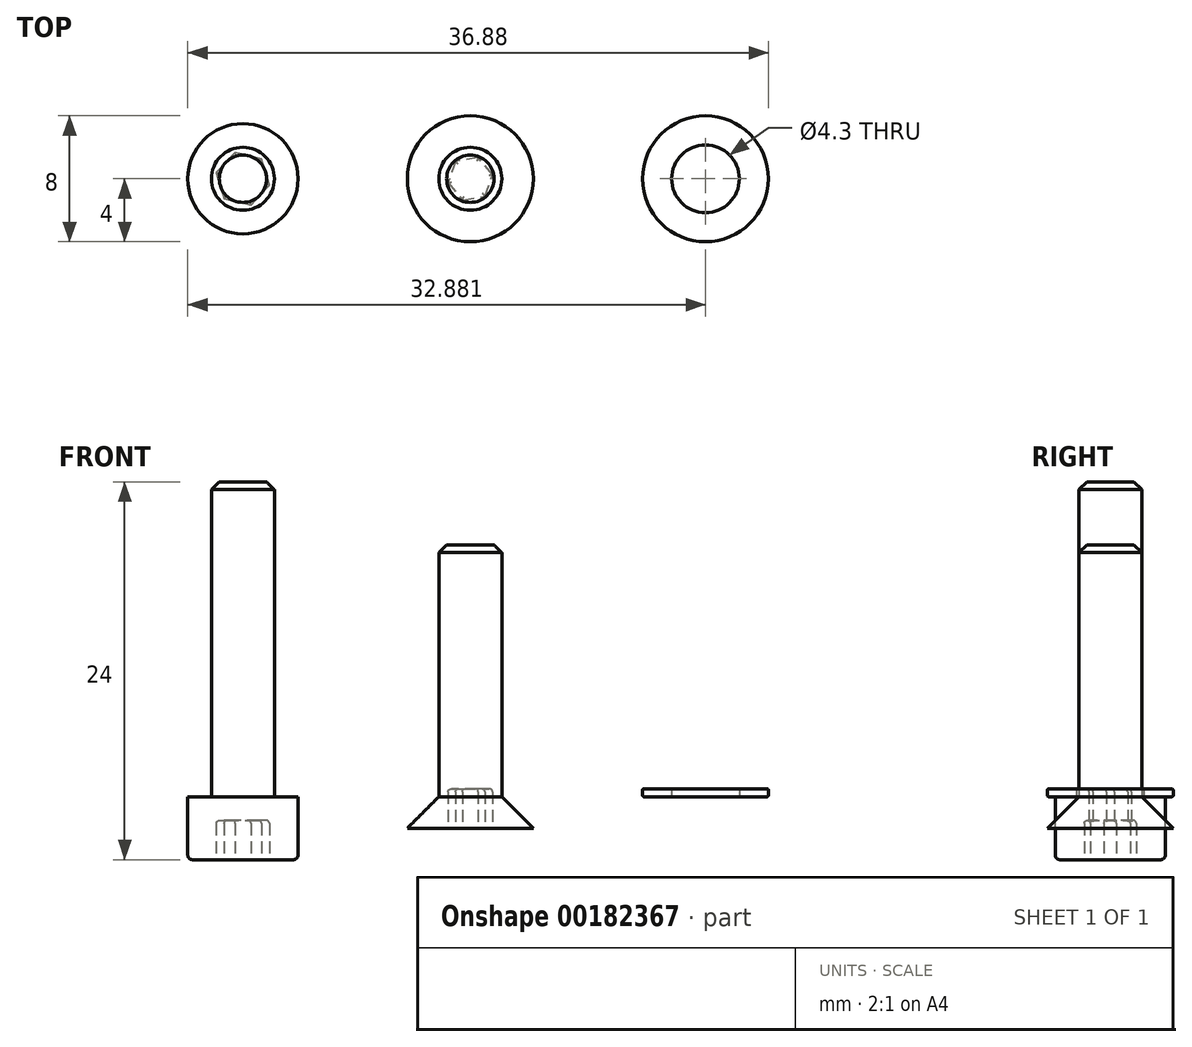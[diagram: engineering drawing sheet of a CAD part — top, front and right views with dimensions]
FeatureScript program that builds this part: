
annotation { "Feature Type Name" : "Feature", "Feature Type Description" : "" }
export const myFeature = defineFeature(function(context is Context, id is Id, definition is map)
    precondition{}
    {
        {
            var Q0;
            Q0=qCreatedBy(makeId("Top.planeOp"),FACE);
            var sketch = newSketch(context, id + "F0", { "sketchPlane" : qUnion([Q0])});
            skCircle(sketch, "E0", {"center": v(0, 0) * mm, "radius": 2 * mm});
            skSolve(sketch);
        }
        {
            var Q0;
            Q0 = qSketchRegion(id + "F0", true);
            extrude(context, id + "F1", {"entities" : qUnion([Q0]), "depth" : 20 * mm});
        }
        {
            var Q0;
            Q0=makeQuery(id+"F1.opExtrude","CAP_FACE",FACE,{"disambiguationData":[OSD([sQuery(id+"F0.wireOp",EDGE,"E0")])],"isStart":false});
            chamfer(context, id + "F2", {"entities" : qUnion([Q0]), "width" : 0.5 * mm, "tangentPropagation" : true});
        }
        {
            var Q0;
            Q0=makeQuery(id+"F1.opExtrude","CAP_FACE",FACE,{"disambiguationData":[OSD([sQuery(id+"F0.wireOp",EDGE,"E0")])],"isStart":true});
            var sketch = newSketch(context, id + "F3", { "sketchPlane" : qUnion([Q0])});
            skCircle(sketch, "E1", {"center": v(0, 0) * mm, "radius": 3.5 * mm});
            skSolve(sketch);
        }
        {
            var Q0;
            Q0 = qSketchRegion(id + "F3", true);
            extrude(context, id + "F4", {"entities" : qUnion([Q0]), "operationType" : NewBodyOperationType.ADD, "depth" : 4 * mm});
        }
        {
            var Q0;
            Q0=makeQuery(id+"F4.opExtrude","CAP_FACE",FACE,{"disambiguationData":[OSD([sQuery(id+"F3.wireOp",EDGE,"E1")])],"isStart":false});
            fillet(context, id + "F5", {"entities" : qUnion([Q0]), "radius" : 0.3 * mm, "tangentPropagation" : true, "allowEdgeOverflow" : false});
        }
        {
            var Q0;
            Q0=makeQuery(id+"F4.opExtrude","CAP_FACE",FACE,{"disambiguationData":[OSD([sQuery(id+"F3.wireOp",EDGE,"E1")])],"isStart":false});
            var sketch = newSketch(context, id + "F6", { "sketchPlane" : qUnion([Q0])});
            skCircle(sketch, "E2.cCircle", {"center": v(0, 0) * mm, "radius": 1.5 * mm, "construction": true});
            skLineSegment(sketch, "E2.0", {"start": v(0.5, 1.66) * mm, "end": v(1.69, 0.4) * mm});
            skLineSegment(sketch, "E2.1", {"start": v(1.69, 0.4) * mm, "end": v(1.18, -1.27) * mm});
            skLineSegment(sketch, "E2.2", {"start": v(1.18, -1.27) * mm, "end": v(-0.5, -1.66) * mm});
            skLineSegment(sketch, "E2.3", {"start": v(-0.5, -1.66) * mm, "end": v(-1.69, -0.4) * mm});
            skLineSegment(sketch, "E2.4", {"start": v(-1.69, -0.4) * mm, "end": v(-1.18, 1.27) * mm});
            skLineSegment(sketch, "E2.5", {"start": v(-1.18, 1.27) * mm, "end": v(0.5, 1.66) * mm});
            skPoint(sketch, "E2.0.midPoint", {"position": v(1.1, 1.02) * mm});
            skSolve(sketch);
        }
        {
            var Q0;
            Q0 = qSketchRegion(id + "F6", true);
            extrude(context, id + "F7", {"entities" : qUnion([Q0]), "operationType" : NewBodyOperationType.REMOVE, "oppositeDirection" : true, "depth" : 2.5 * mm});
        }
        {
            var Q0;
            Q0=makeQuery(id+"F7.boolean.opBoolean","COPY",FACE,{"derivedFrom":makeQuery(id+"F7.opExtrude","CAP_FACE",FACE,{"disambiguationData":[OSD([sQuery(id+"F6.wireOp",EDGE,"E2.0"),sQuery(id+"F6.wireOp",EDGE,"E2.1"),sQuery(id+"F6.wireOp",EDGE,"E2.2"),sQuery(id+"F6.wireOp",EDGE,"E2.3"),sQuery(id+"F6.wireOp",EDGE,"E2.4"),sQuery(id+"F6.wireOp",EDGE,"E2.5")])],"isStart":false})});
            fillet(context, id + "F8", {"entities" : qUnion([Q0]), "radius" : 0.2 * mm, "tangentPropagation" : true, "allowEdgeOverflow" : false});
        }
        {
            var Q0;
            Q0=qCreatedBy(makeId("Top.planeOp"),FACE);
            var sketch = newSketch(context, id + "F9", { "sketchPlane" : qUnion([Q0])});
            skCircle(sketch, "E3", {"center": v(14.44, 0) * mm, "radius": 2 * mm});
            skSolve(sketch);
        }
        {
            var Q0;
            Q0 = qSketchRegion(id + "F9", true);
            extrude(context, id + "F10", {"entities" : qUnion([Q0]), "depth" : 16 * mm});
        }
        {
            var Q0;
            Q0=makeQuery(id+"F10.opExtrude","CAP_FACE",FACE,{"disambiguationData":[OSD([sQuery(id+"F9.wireOp",EDGE,"E3")])],"isStart":false});
            chamfer(context, id + "F11", {"entities" : qUnion([Q0]), "width" : 0.5 * mm, "tangentPropagation" : true});
        }
        {
            var Q0;
            Q0=makeQuery(id+"F10.opExtrude","CAP_FACE",FACE,{"disambiguationData":[OSD([sQuery(id+"F9.wireOp",EDGE,"E3")])],"isStart":true});
            var sketch = newSketch(context, id + "F12", { "sketchPlane" : qUnion([Q0])});
            skCircle(sketch, "E4", {"center": v(14.44, 0) * mm, "radius": 4 * mm});
            skSolve(sketch);
        }
        {
            var Q0;
            Q0 = qSketchRegion(id + "F12", true);
            extrude(context, id + "F13", {"entities" : qUnion([Q0]), "operationType" : NewBodyOperationType.ADD, "depth" : 2 * mm});
        }
        {
            var Q0;
            Q0=makeQuery(id+"F13.opExtrude","CAP_FACE",FACE,{"disambiguationData":[OSD([sQuery(id+"F12.wireOp",EDGE,"E4")])],"isStart":false});
            var sketch = newSketch(context, id + "F14", { "sketchPlane" : qUnion([Q0])});
            skCircle(sketch, "E5.cCircle", {"center": v(14.44, 0) * mm, "radius": 1.25 * mm, "construction": true});
            skLineSegment(sketch, "E5.0", {"start": v(15.87, -0.25) * mm, "end": v(14.94, -1.36) * mm});
            skLineSegment(sketch, "E5.1", {"start": v(14.94, -1.36) * mm, "end": v(13.51, -1.1) * mm});
            skLineSegment(sketch, "E5.2", {"start": v(13.51, -1.1) * mm, "end": v(13.02, 0.25) * mm});
            skLineSegment(sketch, "E5.3", {"start": v(13.02, 0.25) * mm, "end": v(13.95, 1.36) * mm});
            skLineSegment(sketch, "E5.4", {"start": v(13.95, 1.36) * mm, "end": v(15.37, 1.1) * mm});
            skLineSegment(sketch, "E5.5", {"start": v(15.37, 1.1) * mm, "end": v(15.87, -0.25) * mm});
            skPoint(sketch, "E5.0.midPoint", {"position": v(15.4, -0.8) * mm});
            skSolve(sketch);
        }
        {
            var Q0;
            Q0 = qSketchRegion(id + "F14", true);
            extrude(context, id + "F15", {"entities" : qUnion([Q0]), "operationType" : NewBodyOperationType.REMOVE, "oppositeDirection" : true, "depth" : 2.5 * mm});
        }
        {
            var Q0;
            Q0=makeQuery(id+"F15.boolean.opBoolean","COPY",FACE,{"derivedFrom":makeQuery(id+"F15.opExtrude","CAP_FACE",FACE,{"disambiguationData":[OSD([sQuery(id+"F14.wireOp",EDGE,"E5.0"),sQuery(id+"F14.wireOp",EDGE,"E5.1"),sQuery(id+"F14.wireOp",EDGE,"E5.2"),sQuery(id+"F14.wireOp",EDGE,"E5.3"),sQuery(id+"F14.wireOp",EDGE,"E5.4"),sQuery(id+"F14.wireOp",EDGE,"E5.5")])],"isStart":false})});
            fillet(context, id + "F16", {"entities" : qUnion([Q0]), "radius" : 0.2 * mm, "tangentPropagation" : true, "allowEdgeOverflow" : false});
        }
        {
            var Q0;
            Q0=makeQuery(id+"F13.opExtrude","CAP_EDGE",EDGE,{"disambiguationData":[OSD([sQuery(id+"F12.wireOp",EDGE,"E4")])],"isStart":true});
            chamfer(context, id + "F17", {"entities" : qUnion([Q0]), "width" : 2 * mm, "tangentPropagation" : true});
        }
        {
            var Q0;
            Q0=qCreatedBy(makeId("Top.planeOp"),FACE);
            var sketch = newSketch(context, id + "F18", { "sketchPlane" : qUnion([Q0])});
            skCircle(sketch, "E6", {"center": v(29.38, 0) * mm, "radius": 2.15 * mm});
            skCircle(sketch, "E7", {"center": v(29.38, 0) * mm, "radius": 4 * mm});
            skSolve(sketch);
        }
        {
            var Q0;
            Q0 = qSketchRegion(id + "F18", true);
            extrude(context, id + "F19", {"entities" : qUnion([Q0]), "depth" : 0.5 * mm});
        }
        {
            var Q0;
            Q0=makeQuery(id+"F19.opExtrude","CAP_EDGE",EDGE,{"disambiguationData":[OSD([sQuery(id+"F18.wireOp",EDGE,"E7")])],"isStart":true});
            var Q1;
            Q1=makeQuery(id+"F19.opExtrude","CAP_EDGE",EDGE,{"disambiguationData":[OSD([sQuery(id+"F18.wireOp",EDGE,"E7")])],"isStart":false});
            fillet(context, id + "F20", {"entities" : qUnion([Q0, Q1]), "radius" : 0.1 * mm, "tangentPropagation" : true, "allowEdgeOverflow" : false});
        }
    });
